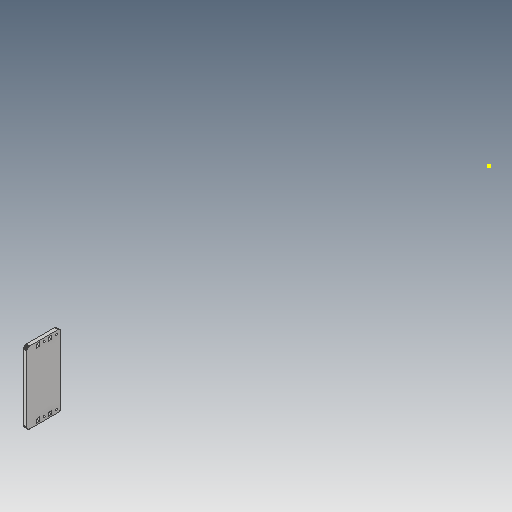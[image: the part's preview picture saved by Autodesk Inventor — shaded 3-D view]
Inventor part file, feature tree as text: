
AUTODESK INVENTOR PART (.ipt)
format: ipt  version: 2017 (Build 210142000, 142)  size: 352,768 bytes
history: native  units: mm
features: sketch x3, other x3, extrude x1, hole x1, reference x1
ambient origin geometry x8: Origin, YZ Plane, XZ Plane, XY Plane, X Axis, Y Axis, Z Axis, Center Point
bodies: Solid1 (feature_tree)
feature tree (9):
  extrude  "Extrusion1"  [1 undecoded]
  hole  "Hole1"  [1 undecoded]
  sketch  "Sketch3"
  sketch  "Sketch1"  dims[d0=6.0mm d1=0.0mm]
  sketch  "Sketch2"  dims[d2=3.2mm d3=6.0mm d4=4.0mm d5=2.0mm d6=90.0deg d7=8.0mm d8=20.594885mm]
  reference  "Reference1"
  parser-record x1  (decoder bookkeeping rows leaked as tree rows — omitted from the tree; the rows remain in map.json)
  other  "Assembly33.iam"
  other  "X Axis Brace_MIR:1"
note: 2 required parameter values undecoded (feature->parameter linkage not recoverable at this tier; creation-order binding heuristic only, values carry confidence <= 0.55)
note: 1 file-system path scrubbed to <path> (originals preserved in map.json)
